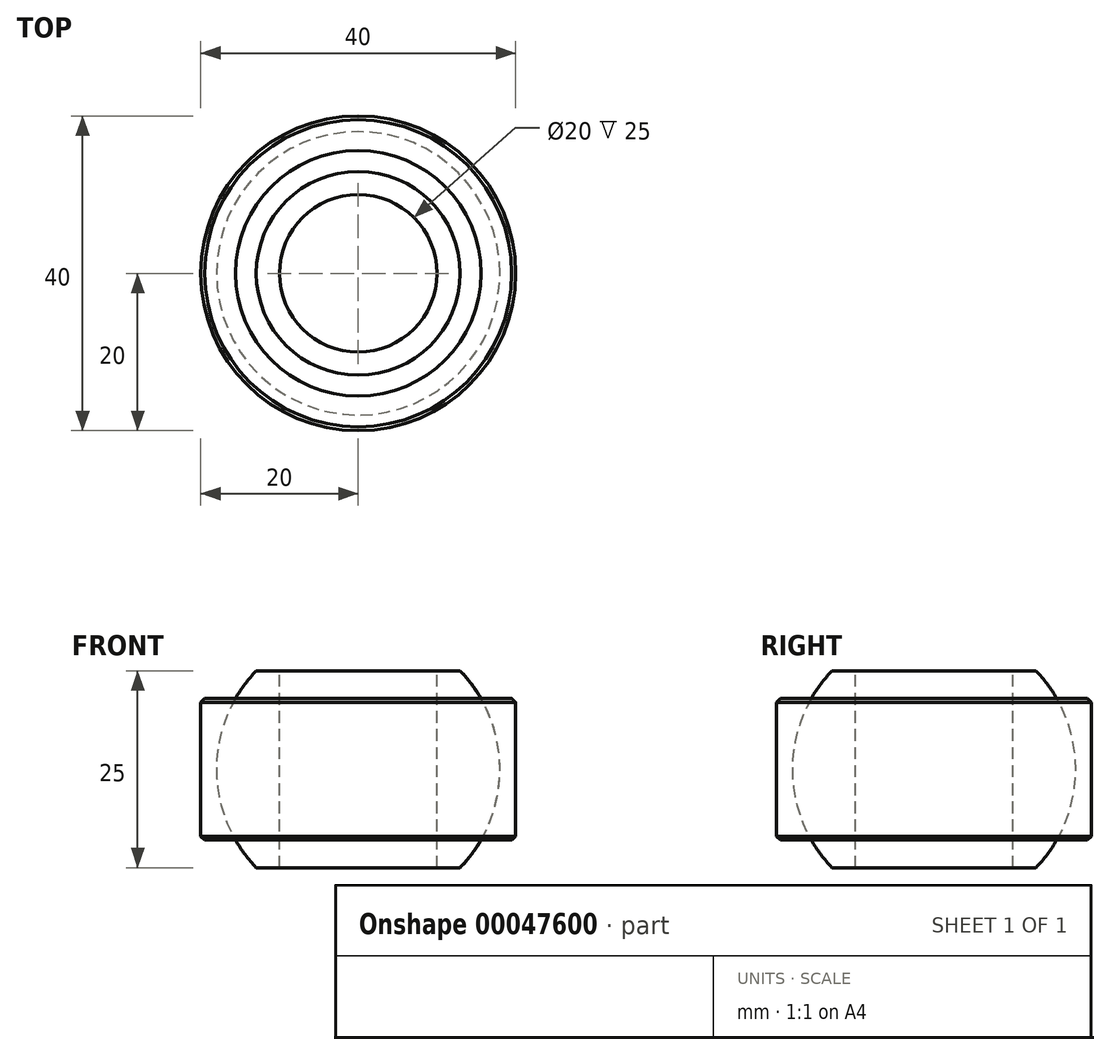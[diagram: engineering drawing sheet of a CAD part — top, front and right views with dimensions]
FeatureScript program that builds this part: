
annotation { "Feature Type Name" : "Feature", "Feature Type Description" : "" }
export const myFeature = defineFeature(function(context is Context, id is Id, definition is map)
    precondition{}
    {
        {
            var Q0;
            Q0=qCreatedBy(makeId("Top.planeOp"),FACE);
            var sketch = newSketch(context, id + "F0", { "sketchPlane" : qUnion([Q0])});
            skCircle(sketch, "E0", {"center": v(0, 0) * mm, "radius": 20 * mm});
            skSolve(sketch);
        }
        {
            var Q0;
            Q0=makeQuery(id+"F0.imprint","IMPRINT",FACE,{"disambiguationData":[TD([[makeQuery(id+"F0.imprint","IMPRINT",EDGE,{"derivedFrom":sQuery(id+"F0.wireOp",EDGE,"E0")}),1.0]])]});
            extrude(context, id + "F1", {"entities" : qUnion([Q0]), "depth" : 18 * mm, "symmetric" : true});
        }
        {
            var Q0;
            Q0=qCreatedBy(makeId("Front.planeOp"),FACE);
            var sketch = newSketch(context, id + "F2", { "sketchPlane" : qUnion([Q0])});
            skArc(sketch, "E1", {"start": v(0, -18) * mm, "mid": v(18, 0) * mm, "end": v(0, 18) * mm});
            skLineSegment(sketch, "E2", {"start": v(0, 32.55) * mm, "end": v(0, -39.65) * mm});
            skSolve(sketch);
        }
        {
            var Q0;
            {var subQ0=sQuery(id+"F2.wireOp",EDGE,"E1");Q0=makeQuery(id+"F2.imprint","IMPRINT",FACE,{"disambiguationData":[TD([[makeQuery(id+"F2.imprint","IMPRINT",EDGE,{"derivedFrom":subQ0}),1.0]])]});}
            var Q1;
            Q1=sQuery(id+"F2.wireOp",EDGE,"E2");
            revolve(context, id + "F3", {"operationType" : NewBodyOperationType.REMOVE, "entities" : qUnion([Q0]), "axis" : qUnion([Q1]), "revolveType" : RevolveType.FULL, "oppositeDirection" : true});
        }
        {
            var Q0;
            {var subQ0=sQuery(id+"F2.wireOp",EDGE,"E1");Q0=makeQuery(id+"F2.imprint","IMPRINT",FACE,{"disambiguationData":[TD([[makeQuery(id+"F2.imprint","IMPRINT",EDGE,{"derivedFrom":subQ0}),1.0]])]});}
            var Q1;
            Q1=sQuery(id+"F2.wireOp",EDGE,"E2");
            revolve(context, id + "F4", {"entities" : qUnion([Q0]), "axis" : qUnion([Q1]), "revolveType" : RevolveType.FULL});
        }
        {
            var Q0;
            Q0=qCreatedBy(makeId("Front.planeOp"),FACE);
            var sketch = newSketch(context, id + "F5", { "sketchPlane" : qUnion([Q0])});
            skLineSegment(sketch, "E3.rect.bottom", {"start": v(25.12, 12.5) * mm, "end": v(-25.12, 12.5) * mm});
            skLineSegment(sketch, "E3.rect.top", {"start": v(25.12, 35.42) * mm, "end": v(-25.12, 35.42) * mm});
            skLineSegment(sketch, "E3.rect.left", {"start": v(25.12, 12.5) * mm, "end": v(25.12, 35.42) * mm});
            skLineSegment(sketch, "E3.rect.right", {"start": v(-25.12, 12.5) * mm, "end": v(-25.12, 35.42) * mm});
            skPoint(sketch, "E3.rect.middle", {"position": v(0, 23.96) * mm});
            skLineSegment(sketch, "E4.rect.bottom", {"start": v(30.75, -12.5) * mm, "end": v(-30.75, -12.5) * mm});
            skLineSegment(sketch, "E4.rect.top", {"start": v(30.75, -55.02) * mm, "end": v(-30.75, -55.02) * mm});
            skLineSegment(sketch, "E4.rect.left", {"start": v(30.75, -12.5) * mm, "end": v(30.75, -55.02) * mm});
            skLineSegment(sketch, "E4.rect.right", {"start": v(-30.75, -12.5) * mm, "end": v(-30.75, -55.02) * mm});
            skPoint(sketch, "E4.rect.middle", {"position": v(0, -33.76) * mm});
            skSolve(sketch);
        }
        {
            var Q0;
            Q0=makeQuery(id+"F5.imprint","IMPRINT",FACE,{"disambiguationData":[TD([[makeQuery(id+"F5.imprint","IMPRINT",EDGE,{"derivedFrom":sQuery(id+"F5.wireOp",EDGE,"E4.rect.bottom")}),1.0]])]});
            var Q1;
            Q1=makeQuery(id+"F5.imprint","IMPRINT",FACE,{"disambiguationData":[TD([[makeQuery(id+"F5.imprint","IMPRINT",EDGE,{"derivedFrom":sQuery(id+"F5.wireOp",EDGE,"E3.rect.bottom")}),-1.0]])]});
            extrude(context, id + "F6", {"entities" : qUnion([Q0, Q1]), "operationType" : NewBodyOperationType.REMOVE, "endBound" : BoundingType.THROUGH_ALL, "oppositeDirection" : true, "depth" : 25 * mm, "hasSecondDirection" : true, "secondDirectionBound" : BoundingType.THROUGH_ALL, "secondDirectionOppositeDirection" : false, "secondDirectionDepth" : 25 * mm});
        }
        {
            var Q0;
            Q0=makeQuery(id+"F6.boolean.opBoolean","COPY",FACE,{"derivedFrom":makeQuery(id+"F6.opExtrude","SWEPT_FACE",FACE,{"disambiguationData":[OSD([sQuery(id+"F5.wireOp",EDGE,"E3.rect.bottom")])]})});
            var sketch = newSketch(context, id + "F7", { "sketchPlane" : qUnion([Q0])});
            skCircle(sketch, "E5", {"center": v(0, 0) * mm, "radius": 10 * mm});
            skSolve(sketch);
        }
        {
            var Q0;
            Q0=makeQuery(id+"F7.imprint","IMPRINT",FACE,{"disambiguationData":[TD([[makeQuery(id+"F7.imprint","IMPRINT",EDGE,{"derivedFrom":sQuery(id+"F7.wireOp",EDGE,"E5")}),1.0]])]});
            extrude(context, id + "F8", {"entities" : qUnion([Q0]), "operationType" : NewBodyOperationType.REMOVE, "endBound" : BoundingType.THROUGH_ALL, "oppositeDirection" : true, "depth" : 25 * mm});
        }
        {
            var Q0;
            Q0=makeQuery(id+"F1.opExtrude","CAP_EDGE",EDGE,{"disambiguationData":[OSD([sQuery(id+"F0.wireOp",EDGE,"E0")])],"isStart":false});
            var Q1;
            Q1=makeQuery(id+"F1.opExtrude","CAP_EDGE",EDGE,{"disambiguationData":[OSD([sQuery(id+"F0.wireOp",EDGE,"E0")])],"isStart":true});
            chamfer(context, id + "F9", {"entities" : qUnion([Q0, Q1]), "width" : 0.5 * mm, "tangentPropagation" : true});
        }
    });
